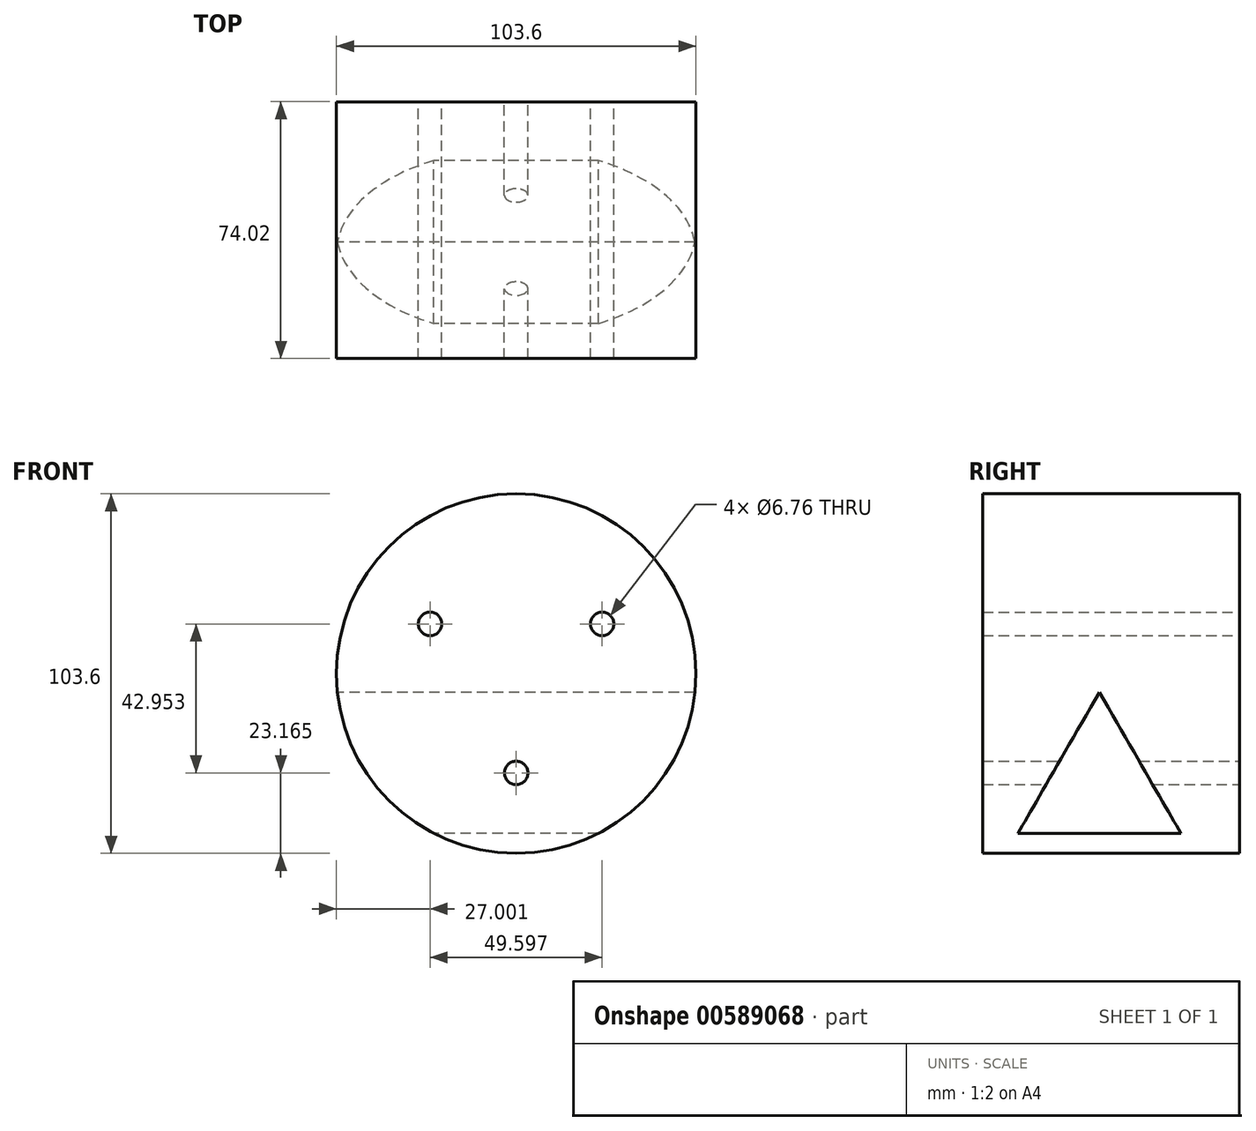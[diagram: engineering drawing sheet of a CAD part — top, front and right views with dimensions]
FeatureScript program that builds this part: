
annotation { "Feature Type Name" : "Feature", "Feature Type Description" : "" }
export const myFeature = defineFeature(function(context is Context, id is Id, definition is map)
    precondition{}
    {
        {
            var Q0;
            Q0=qCreatedBy(makeId("Top.planeOp"),FACE);
            var sketch = newSketch(context, id + "F0", { "sketchPlane" : qUnion([Q0])});
            skLineSegment(sketch, "E0.bottom", {"start": v(0, 40.43) * mm, "end": v(-51.8, 40.43) * mm});
            skLineSegment(sketch, "E0.top", {"start": v(0, -33.6) * mm, "end": v(-51.8, -33.6) * mm});
            skLineSegment(sketch, "E0.left", {"start": v(0, 40.43) * mm, "end": v(0, -33.6) * mm});
            skLineSegment(sketch, "E0.right", {"start": v(-51.8, 40.43) * mm, "end": v(-51.8, -33.6) * mm});
            skSolve(sketch);
        }
        {
            var Q0;
            Q0 = qSketchRegion(id + "F0", true);
            var Q1;
            Q1=sQuery(id+"F0.wireOp",EDGE,"E0.left");
            revolve(context, id + "F1", {"entities" : qUnion([Q0]), "axis" : qUnion([Q1]), "revolveType" : RevolveType.FULL});
        }
        {
            var Q0;
            Q0=makeQuery(id+"F1.opRevolve","SWEPT_FACE",FACE,{"disambiguationData":[OSD([sQuery(id+"F0.wireOp",EDGE,"E0.bottom")])]});
            var sketch = newSketch(context, id + "F2", { "sketchPlane" : qUnion([Q0])});
            skCircle(sketch, "E1", {"center": v(0, -28.64) * mm, "radius": 14.52 * mm});
            skCircle(sketch, "E2.1.0", {"center": v(24.8, 14.32) * mm, "radius": 14.52 * mm});
            skCircle(sketch, "E2.2.0", {"center": v(-24.8, 14.32) * mm, "radius": 14.52 * mm});
            skPoint(sketch, "E2.center", {"position": v(0, 0) * mm});
            skSolve(sketch);
        }
        {
            var Q0;
            Q0=sQuery(id+"F2.wireOp",VERTEX,"E2.2.0.center");
            var Q1;
            Q1=sQuery(id+"F2.wireOp",VERTEX,"E1.center");
            var Q2;
            Q2=sQuery(id+"F2.wireOp",VERTEX,"E2.1.0.center");
            var Q3;
            Q3=makeQuery(id+"F1.opRevolve","SWEPT_BODY",BODY,{"disambiguationData":[OSD([sQuery(id+"F0.wireOp",EDGE,"E0.bottom"),sQuery(id+"F0.wireOp",EDGE,"E0.top"),sQuery(id+"F0.wireOp",EDGE,"E0.left"),sQuery(id+"F0.wireOp",EDGE,"E0.right")])]});
            hole(context, id + "F3", {"style" : HoleStyle.SIMPLE, "endStyle" : HoleEndStyle.THROUGH, "standardTappedOrClearance" : lookupTablePath({ "fit" : "Normal (ASME)", "standard" : "ANSI", "size" : "1/4", "type" : "Clearance" }), "standardBlindInLast" : lookupTablePath({ "fit" : "Free", "standard" : "ANSI", "size" : "1/4", "type" : "Clearance" }), "holeDiameter" : 6.76 * mm, "majorDiameter" : 6.35 * mm, "isTappedThrough" : true, "tappedDepth" : 12.7 * mm, "tapClearance" : 3, "locations" : qUnion([Q0, Q1, Q2]), "scope" : qUnion([Q3])});
        }
        {
            var Q0;
            Q0=qCreatedBy(makeId("Right.planeOp"),FACE);
            var sketch = newSketch(context, id + "F4", { "sketchPlane" : qUnion([Q0])});
            skCircle(sketch, "E3.cCircle", {"center": v(0, -32.5) * mm, "radius": 13.55 * mm, "construction": true});
            skLineSegment(sketch, "E3.0", {"start": v(23.47, -46.04) * mm, "end": v(-23.47, -46.04) * mm});
            skLineSegment(sketch, "E3.1", {"start": v(-23.47, -46.04) * mm, "end": v(0, -5.38) * mm});
            skLineSegment(sketch, "E3.2", {"start": v(0, -5.38) * mm, "end": v(23.47, -46.04) * mm});
            skPoint(sketch, "E3.0.midPoint", {"position": v(0, -46.04) * mm});
            skSolve(sketch);
        }
        {
            var Q0;
            Q0 = qSketchRegion(id + "F4", true);
            extrude(context, id + "F5", {"entities" : qUnion([Q0]), "operationType" : NewBodyOperationType.REMOVE, "endBound" : BoundingType.THROUGH_ALL, "depth" : 25.4 * mm, "offsetDistance" : 25.4 * mm, "hasSecondDirection" : true, "secondDirectionBound" : SecondDirectionBoundingType.THROUGH_ALL, "secondDirectionOppositeDirection" : true, "secondDirectionDepth" : 25.4 * mm});
        }
    });
